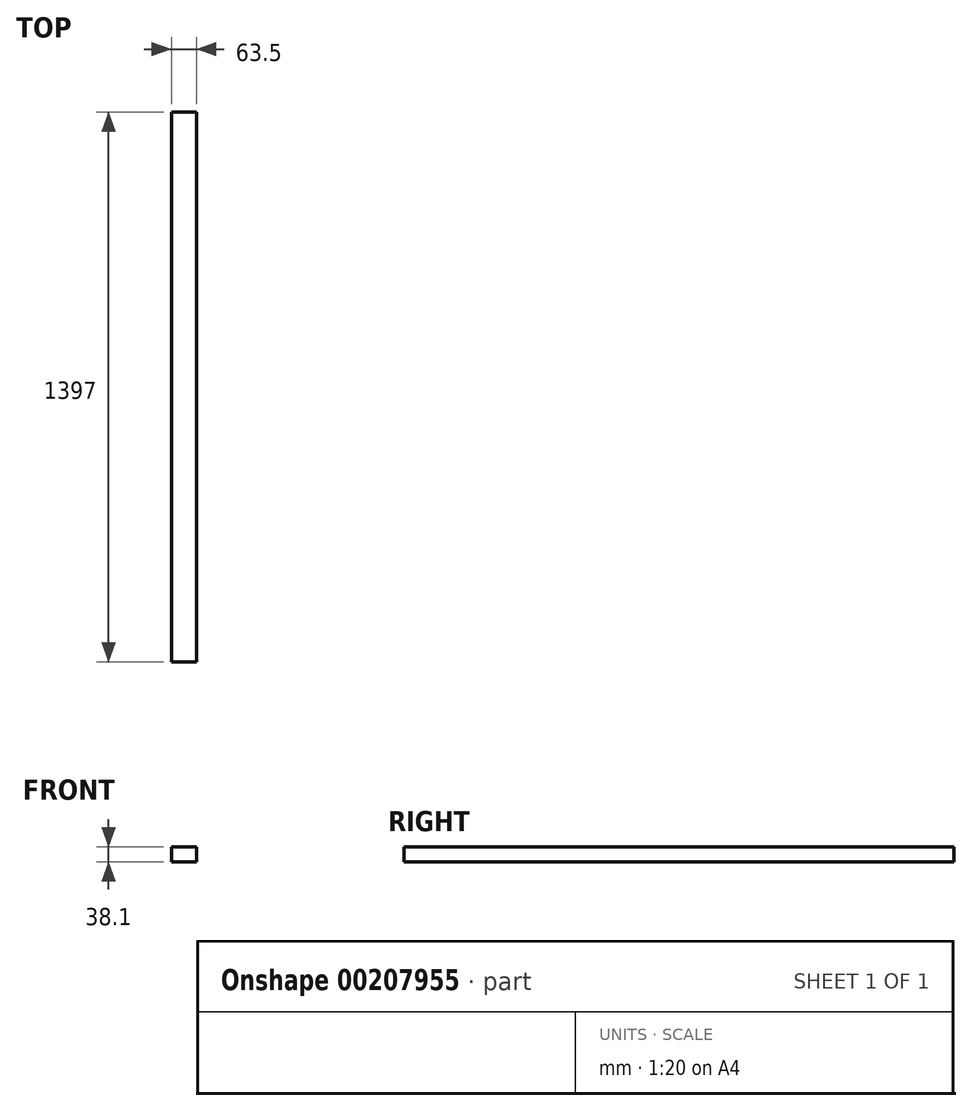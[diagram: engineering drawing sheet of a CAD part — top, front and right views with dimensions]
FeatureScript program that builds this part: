
annotation { "Feature Type Name" : "Feature", "Feature Type Description" : "" }
export const myFeature = defineFeature(function(context is Context, id is Id, definition is map)
    precondition{}
    {
        {
            var Q0;
            Q0=qCreatedBy(makeId("Front.planeOp"),FACE);
            var sketch = newSketch(context, id + "F0", { "sketchPlane" : qUnion([Q0])});
            skLineSegment(sketch, "E0.bottom", {"start": v(0, 0) * mm, "end": v(63.5, 0) * mm});
            skLineSegment(sketch, "E0.top", {"start": v(0, 38.1) * mm, "end": v(63.5, 38.1) * mm});
            skLineSegment(sketch, "E0.left", {"start": v(0, 0) * mm, "end": v(0, 38.1) * mm});
            skLineSegment(sketch, "E0.right", {"start": v(63.5, 0) * mm, "end": v(63.5, 38.1) * mm});
            skSolve(sketch);
        }
        {
            var Q0;
            Q0 = qSketchRegion(id + "F0", true);
            extrude(context, id + "F1", {"entities" : qUnion([Q0]), "depth" : 1397 * mm});
        }
    });
